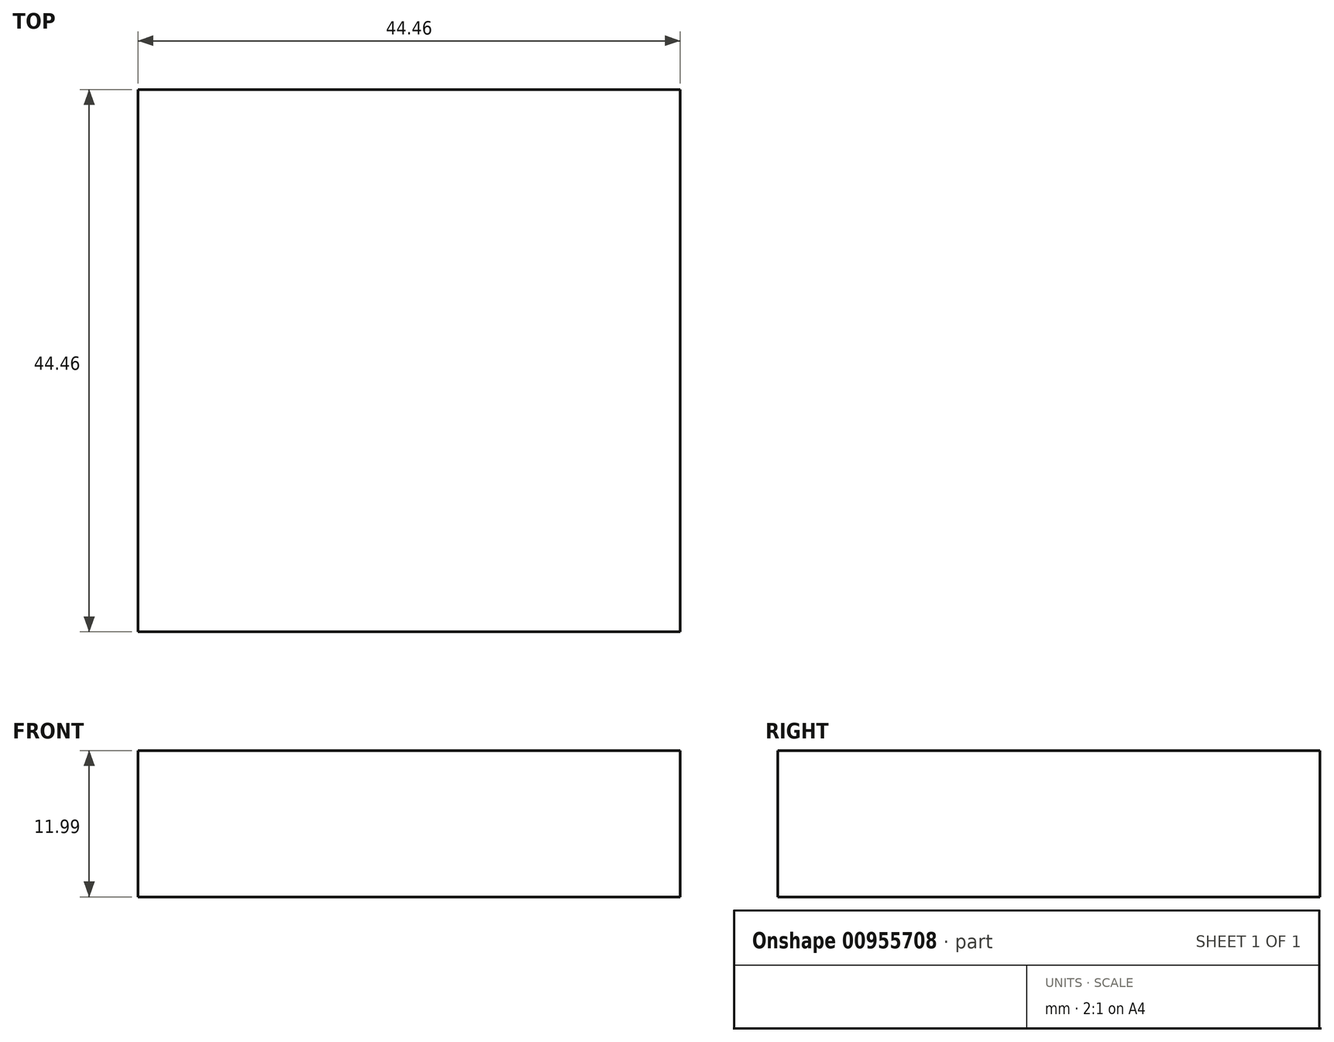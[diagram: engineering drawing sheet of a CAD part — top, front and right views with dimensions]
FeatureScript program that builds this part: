
annotation { "Feature Type Name" : "Feature", "Feature Type Description" : "" }
export const myFeature = defineFeature(function(context is Context, id is Id, definition is map)
    precondition{}
    {
        {
            var Q0;
            Q0=qCreatedBy(makeId("Top.planeOp"),FACE);
            var sketch = newSketch(context, id + "F0", { "sketchPlane" : qUnion([Q0])});
            skLineSegment(sketch, "E0.bottom", {"start": v(22.23, -22.22) * mm, "end": v(-22.23, -22.23) * mm});
            skLineSegment(sketch, "E0.top", {"start": v(22.23, 22.23) * mm, "end": v(-22.23, 22.22) * mm});
            skLineSegment(sketch, "E0.left", {"start": v(22.23, -22.22) * mm, "end": v(22.23, 22.23) * mm});
            skLineSegment(sketch, "E0.right", {"start": v(-22.23, -22.23) * mm, "end": v(-22.23, 22.22) * mm});
            skPoint(sketch, "E0.middle", {"position": v(0, 0) * mm});
            skSolve(sketch);
        }
        {
            var Q0;
            Q0 = qSketchRegion(id + "F0", true);
            extrude(context, id + "F1", {"entities" : qUnion([Q0]), "depth" : 12 * mm, "offsetDistance" : 25.4 * mm});
        }
    });
